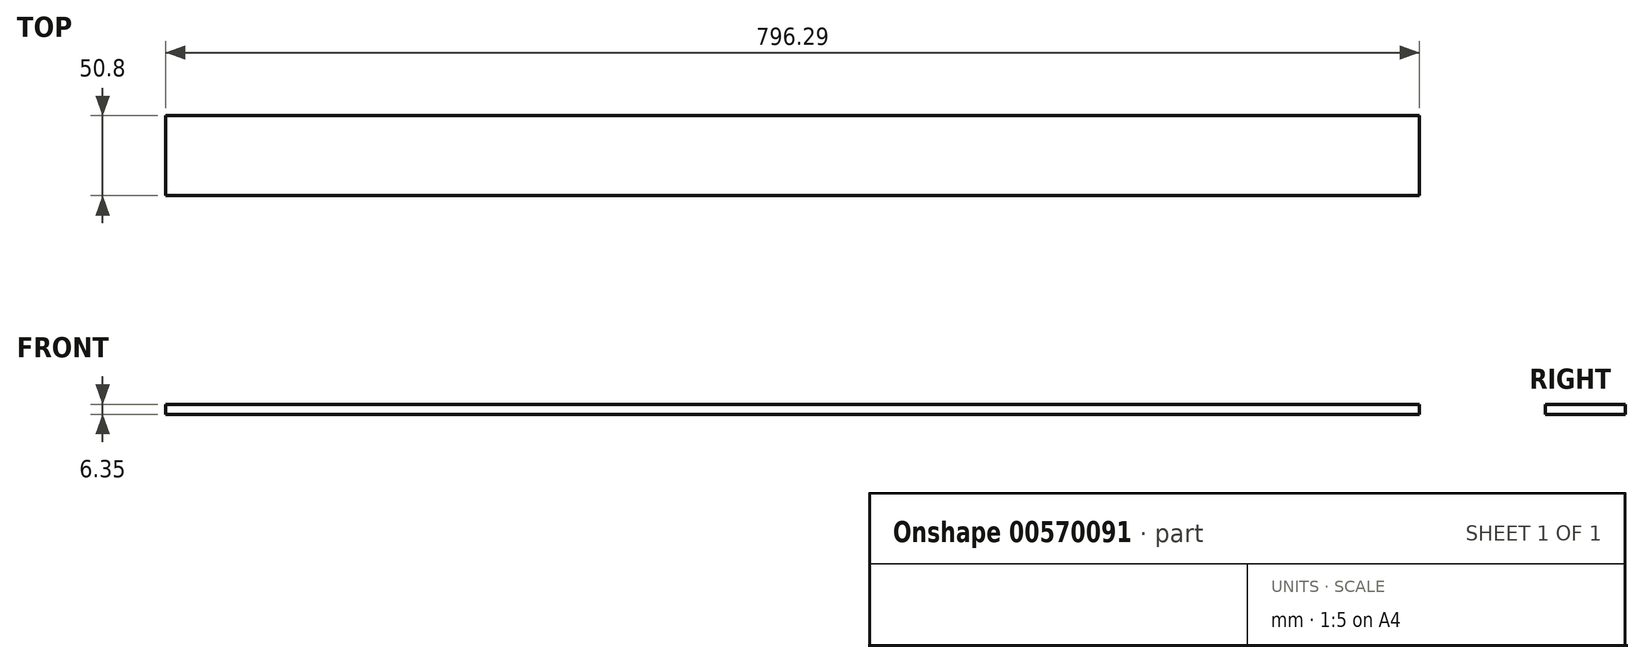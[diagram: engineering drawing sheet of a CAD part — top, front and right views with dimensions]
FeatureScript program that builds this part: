
annotation { "Feature Type Name" : "Feature", "Feature Type Description" : "" }
export const myFeature = defineFeature(function(context is Context, id is Id, definition is map)
    precondition{}
    {
        {
            var Q0;
            Q0=qCreatedBy(makeId("Right.planeOp"),FACE);
            var sketch = newSketch(context, id + "F0", { "sketchPlane" : qUnion([Q0])});
            skLineSegment(sketch, "E0", {"start": v(0, 0) * mm, "end": v(50.8, 0) * mm});
            skLineSegment(sketch, "E1", {"start": v(0, 0) * mm, "end": v(0, 796.3) * mm});
            skLineSegment(sketch, "E2", {"start": v(0, 796.3) * mm, "end": v(50.8, 796.3) * mm});
            skLineSegment(sketch, "E3", {"start": v(50.8, 796.3) * mm, "end": v(50.8, 0) * mm});
            skSolve(sketch);
        }
        {
            var Q0;
            Q0 = qSketchRegion(id + "F0", true);
            extrude(context, id + "F1", {"entities" : qUnion([Q0]), "depth" : 6.35 * mm, "offsetDistance" : 25.4 * mm});
        }
        {
            var Q0;
            Q0=makeQuery(id+"F1.opExtrude","SWEPT_BODY",BODY,{"disambiguationData":[OSD([sQuery(id+"F0.wireOp",EDGE,"E0"),sQuery(id+"F0.wireOp",EDGE,"E1"),sQuery(id+"F0.wireOp",EDGE,"E2"),sQuery(id+"F0.wireOp",EDGE,"E3")])]});
            var Q1;
            Q1=makeQuery(id+"F1.opExtrude","CAP_EDGE",EDGE,{"disambiguationData":[OSD([sQuery(id+"F0.wireOp",EDGE,"E0")])],"isStart":true});
            transform(context, id + "F2", {"entities" : qUnion([Q0]), "transformType" : TransformType.ROTATION, "transformAxis" : qUnion([Q1]), "angle" : 90 * degree, "makeCopy" : false});
        }
    });
